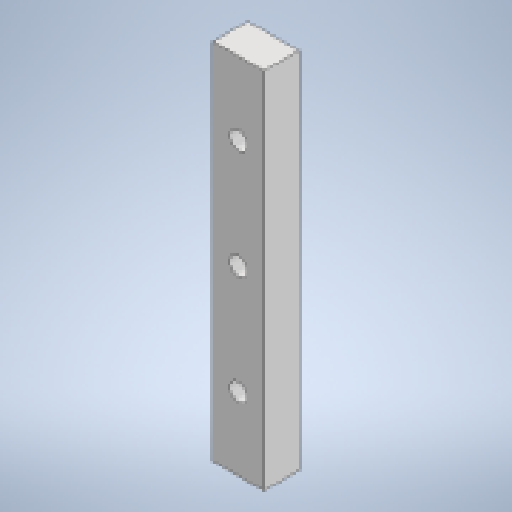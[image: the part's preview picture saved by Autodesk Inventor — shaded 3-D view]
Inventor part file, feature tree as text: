
AUTODESK INVENTOR PART (.ipt)
format: ipt  version: 2024.1 (Build 281209000, 209)  size: 258,048 bytes
history: native  units: in
note: dims shown in document units (in); Inventor stores cm internally (conversion verified against a paired STEP export)
features: extrude x3, sketch x3
ambient origin geometry x8: Origin, YZ Plane, XZ Plane, XY Plane, X Axis, Y Axis, Z Axis, Center Point
bodies: Solid1 (feature_tree)
feature tree (6):
  extrude  "Extrusion1"  Depth=0.2756in
  extrude  "Extrusion2"  Depth=1.9685in
  extrude  "Extrusion3"  Depth=0.0906in
  sketch  "Sketch1"  dims[d0=0.189in d1=0.2756in]
  sketch  "Sketch2"  dims[d2=1.9685in d3=0.0in d4=0.0945in]
  sketch  "Sketch3"  dims[d5=0.3937in d6=0.1378in d7=1.1811in d9=0.5906in d10=0.3937in d12=0.3937in d14=0.0in d15=0.0in d16=0.1654in d17=0.1654in d18=0.1654in d19=0.0906in d20=0.0in]
